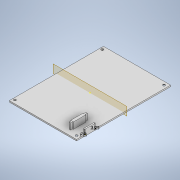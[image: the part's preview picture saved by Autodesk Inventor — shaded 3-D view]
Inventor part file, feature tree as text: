
AUTODESK INVENTOR PART (.ipt)
format: ipt  version: 2020.1 (Build 241239000, 239)  size: 186,368 bytes
history: native  units: mm
features: sketch x7, extrude x4, hole x2, plane x1, mirror x1
ambient origin geometry x8: Origin, YZ Plane, XZ Plane, XY Plane, X Axis, Y Axis, Z Axis, Center Point
bodies: Solid1 (feature_tree)
feature tree (15):
  extrude  "Extrusion1"  Depth=120.0mm
  extrude  "Extrusion2"  Depth=2.4mm
  extrude  "Extrusion3"  Depth=15.25mm
  extrude  "Extrusion4"  Depth=1.25mm
  plane  "Work Plane3"
  hole  "Hole1"  [1 undecoded]
  sketch  "Sketch12"  dims[d12=2.5mm d13=8.25mm d14=0.0mm]
  hole  "Hole2"  [1 undecoded]
  mirror  "Mirror4"
  sketch  "Sketch1"  dims[d0=168.0mm d1=120.0mm]
  sketch  "Sketch2"  dims[d2=2.4mm d3=0.0mm d4=2.4mm]
  sketch  "Sketch3"  dims[d5=17.5mm d6=15.25mm]
  sketch  "Sketch4"  dims[d7=8.25mm d8=0.0mm d9=1.25mm]
  sketch  "Sketch11"  dims[d10=2.5mm d11=1.25mm]
  sketch  "Sketch13"  dims[d15=18.5mm d16=13.0mm d17=5.0mm d18=22.0mm d19=11.25mm d20=0.0mm d21=2.625mm d22=8.0mm d23=2.625mm d24=8.0mm d63=6.0mm d64=4.0mm d65=4.0mm d66=6.0mm d67=4.0mm d68=6.0mm d69=8.4mm d70=2.0mm d71=90.0deg d72=8.0mm d73=20.594885mm d74=6.0mm d75=6.0mm d76=4.0mm d77=6.0mm d78=8.4mm d79=2.0mm d80=90.0deg d81=10.0mm d82=20.594885mm]
note: 2 required parameter values undecoded (feature->parameter linkage not recoverable at this tier; creation-order binding heuristic only, values carry confidence <= 0.55)
